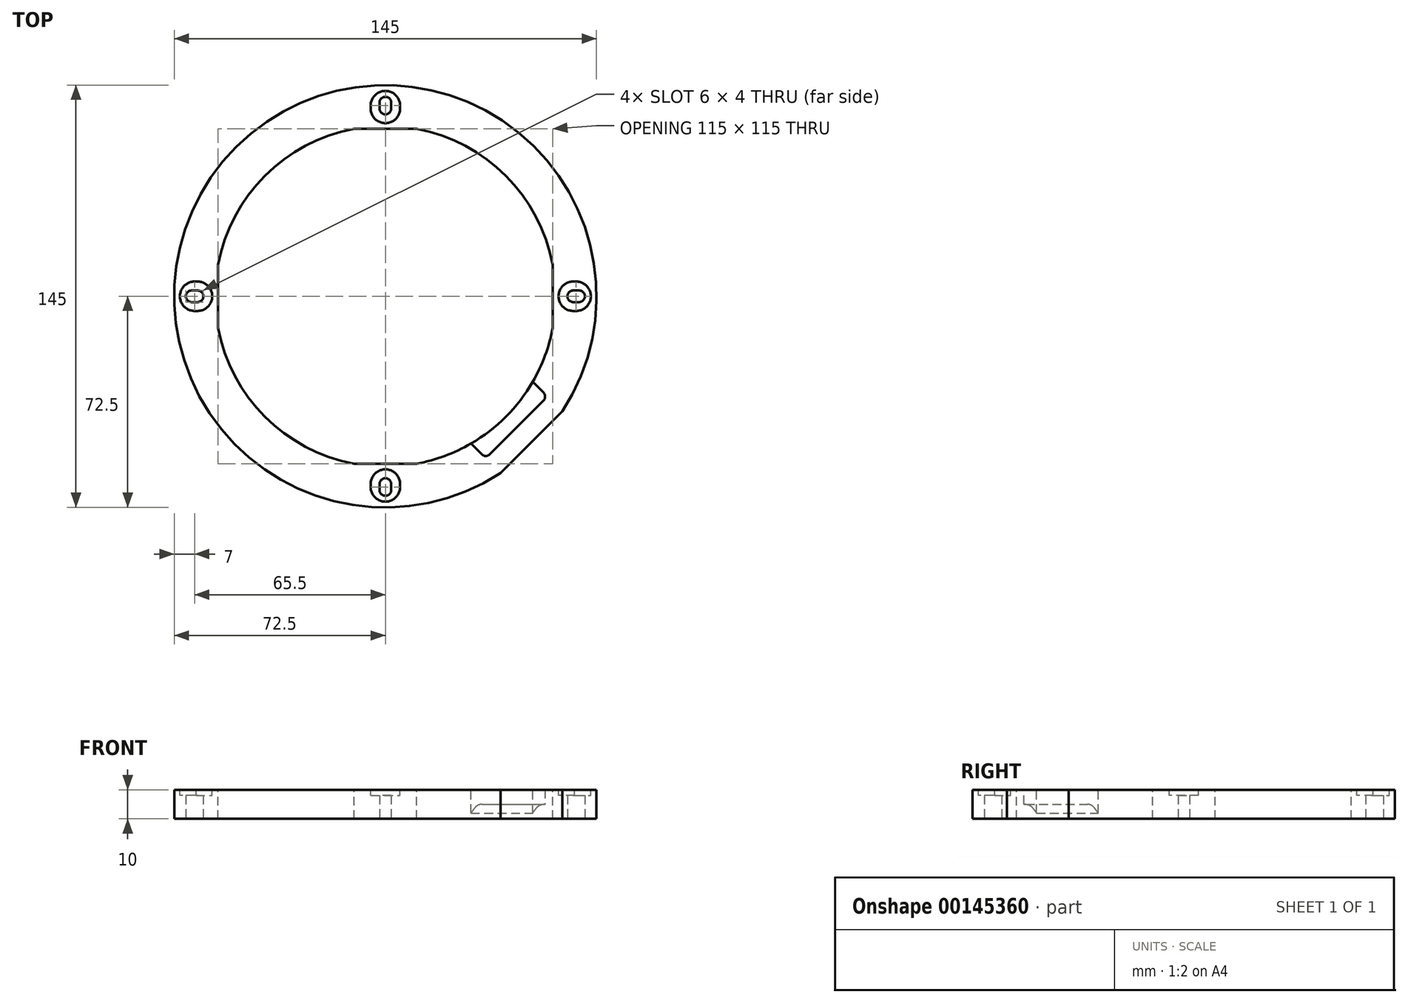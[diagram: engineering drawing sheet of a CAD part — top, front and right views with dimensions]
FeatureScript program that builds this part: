
annotation { "Feature Type Name" : "Feature", "Feature Type Description" : "" }
export const myFeature = defineFeature(function(context is Context, id is Id, definition is map)
    precondition{}
    {
        {
            var Q0;
            Q0=qCreatedBy(makeId("Top.planeOp"),FACE);
            var sketch = newSketch(context, id + "F0", { "sketchPlane" : qUnion([Q0])});
            skCircle(sketch, "E0", {"center": v(0, 0) * mm, "radius": 72.5 * mm});
            skCircle(sketch, "E1.0", {"center": v(0, 0) * mm, "radius": 58.5 * mm});
            skLineSegment(sketch, "E2", {"start": v(-72.5, 0) * mm, "end": v(-58.5, 0) * mm, "construction": true});
            skCircle(sketch, "E3", {"center": v(-65.5, 0) * mm, "radius": 2 * mm});
            skLineSegment(sketch, "E4", {"start": v(-67.5, 0) * mm, "end": v(-65.5, 0) * mm, "construction": true});
            skLineSegment(sketch, "E5", {"start": v(-65.5, 0) * mm, "end": v(-63.5, 0) * mm, "construction": true});
            skCircle(sketch, "E6", {"center": v(-66.5, 0) * mm, "radius": 2 * mm});
            skCircle(sketch, "E7", {"center": v(-64.5, 0) * mm, "radius": 2 * mm});
            skLineSegment(sketch, "E8.bottom", {"start": v(-64.5, 2) * mm, "end": v(-66.5, 2) * mm});
            skLineSegment(sketch, "E8.top", {"start": v(-64.5, -2) * mm, "end": v(-66.5, -2) * mm});
            skLineSegment(sketch, "E8.left", {"start": v(-64.5, 2) * mm, "end": v(-64.5, -2) * mm});
            skLineSegment(sketch, "E8.right", {"start": v(-66.5, 2) * mm, "end": v(-66.5, -2) * mm});
            skCircle(sketch, "E9.1.0", {"center": v(0, -66.5) * mm, "radius": 2 * mm});
            skCircle(sketch, "E9.1.1", {"center": v(0, -64.5) * mm, "radius": 2 * mm});
            skLineSegment(sketch, "E9.1.2", {"start": v(-2, -64.5) * mm, "end": v(-2, -66.5) * mm});
            skLineSegment(sketch, "E9.1.3", {"start": v(2, -64.5) * mm, "end": v(2, -66.5) * mm});
            skCircle(sketch, "E9.2.0", {"center": v(66.5, 0) * mm, "radius": 2 * mm});
            skCircle(sketch, "E9.2.1", {"center": v(64.5, 0) * mm, "radius": 2 * mm});
            skLineSegment(sketch, "E9.2.2", {"start": v(64.5, -2) * mm, "end": v(66.5, -2) * mm});
            skLineSegment(sketch, "E9.2.3", {"start": v(64.5, 2) * mm, "end": v(66.5, 2) * mm});
            skCircle(sketch, "E9.3.0", {"center": v(0, 66.5) * mm, "radius": 2 * mm});
            skCircle(sketch, "E9.3.1", {"center": v(0, 64.5) * mm, "radius": 2 * mm});
            skLineSegment(sketch, "E9.3.2", {"start": v(2, 64.5) * mm, "end": v(2, 66.5) * mm});
            skLineSegment(sketch, "E9.3.3", {"start": v(-2, 64.5) * mm, "end": v(-2, 66.5) * mm});
            skSolve(sketch);
        }
        {
            var Q0;
            Q0=makeQuery(id+"F0.imprint","IMPRINT",FACE,{"disambiguationData":[TD([[makeQuery(id+"F0.imprint","IMPRINT",EDGE,{"derivedFrom":sQuery(id+"F0.wireOp",EDGE,"E0")}),1.0]])]});
            extrude(context, id + "F1", {"entities" : qUnion([Q0]), "depth" : 10 * mm});
        }
        {
            var Q0;
            Q0=makeQuery(id+"F1.opExtrude","CAP_FACE",FACE,{"disambiguationData":[OSD([sQuery(id+"F0.wireOp",EDGE,"E0"),sQuery(id+"F0.wireOp",EDGE,"E1.0")])],"isStart":false});
            var sketch = newSketch(context, id + "F2", { "sketchPlane" : qUnion([Q0])});
            skLineSegment(sketch, "E10", {"start": v(0, 0) * mm, "end": v(51.27, -51.27) * mm, "construction": true});
            skLineSegment(sketch, "E11", {"start": v(40.66, -61.87) * mm, "end": v(61.87, -40.66) * mm});
            skLineSegment(sketch, "E12", {"start": v(40.66, -61.87) * mm, "end": v(39.55, -60.76) * mm});
            skLineSegment(sketch, "E13", {"start": v(39.55, -60.76) * mm, "end": v(60.76, -39.55) * mm});
            skLineSegment(sketch, "E14", {"start": v(60.76, -39.55) * mm, "end": v(61.87, -40.66) * mm});
            skSolve(sketch);
        }
        {
            var Q0;
            Q0 = qSketchRegion(id + "F2", true);
            var Q1;
            {var subQ0=sQuery(id+"F2.wireOp",EDGE,"E13");Q1=makeQuery(id+"F2.imprint","IMPRINT",FACE,{"disambiguationData":[TD([[makeQuery(id+"F2.imprint","IMPRINT",EDGE,{"derivedFrom":subQ0}),-1.0]])]});}
            extrude(context, id + "F3", {"entities" : qUnion([Q0, Q1]), "operationType" : NewBodyOperationType.REMOVE, "endBound" : BoundingType.THROUGH_ALL, "oppositeDirection" : true, "depth" : 25 * mm});
        }
        {
            var Q0;
            Q0=makeQuery(id+"F1.opExtrude","CAP_FACE",FACE,{"disambiguationData":[OSD([sQuery(id+"F0.wireOp",EDGE,"E0"),sQuery(id+"F0.wireOp",EDGE,"E1.0")])],"isStart":false});
            var sketch = newSketch(context, id + "F4", { "sketchPlane" : qUnion([Q0])});
            skLineSegment(sketch, "E15", {"start": v(60.76, -39.55) * mm, "end": v(50.59, -29.38) * mm, "construction": true});
            skLineSegment(sketch, "E16", {"start": v(50.59, -29.38) * mm, "end": v(29.38, -50.59) * mm});
            skLineSegment(sketch, "E17", {"start": v(29.38, -50.59) * mm, "end": v(39.55, -60.76) * mm, "construction": true});
            skLineSegment(sketch, "E18", {"start": v(39.55, -60.76) * mm, "end": v(60.76, -39.55) * mm, "construction": true});
            skLineSegment(sketch, "E19", {"start": v(34.46, -55.68) * mm, "end": v(55.68, -34.46) * mm});
            skLineSegment(sketch, "E20", {"start": v(55.68, -34.46) * mm, "end": v(50.59, -29.38) * mm});
            skLineSegment(sketch, "E21", {"start": v(34.46, -55.68) * mm, "end": v(29.38, -50.59) * mm});
            skSolve(sketch);
        }
        {
            var Q0;
            Q0 = qSketchRegion(id + "F4", true);
            extrude(context, id + "F5", {"entities" : qUnion([Q0]), "operationType" : NewBodyOperationType.REMOVE, "oppositeDirection" : true, "depth" : 5 * mm});
        }
        {
            var Q0;
            Q0=makeQuery(id+"F1.opExtrude","CAP_FACE",FACE,{"disambiguationData":[OSD([sQuery(id+"F0.wireOp",EDGE,"E0"),sQuery(id+"F0.wireOp",EDGE,"E1.0")])],"isStart":false});
            var sketch = newSketch(context, id + "F6", { "sketchPlane" : qUnion([Q0])});
            skCircle(sketch, "E22", {"center": v(-65.5, 0) * mm, "radius": 5.05 * mm});
            skPoint(sketch, "E22.centerSnap0", {"position": v(-62.5, 0) * mm});
            skPoint(sketch, "E22.centerSnap1", {"position": v(-65.5, 2) * mm});
            skCircle(sketch, "E23", {"center": v(0, 65.5) * mm, "radius": 5.05 * mm});
            skPoint(sketch, "E23.centerSnap0", {"position": v(-2, 65.5) * mm});
            skCircle(sketch, "E24", {"center": v(65.5, 0) * mm, "radius": 5.05 * mm});
            skPoint(sketch, "E24.centerSnap0", {"position": v(65.5, 2) * mm});
            skCircle(sketch, "E25", {"center": v(0, -65.5) * mm, "radius": 5.05 * mm});
            skPoint(sketch, "E25.centerSnap0", {"position": v(-2, -65.5) * mm});
            skPoint(sketch, "E25.centerSnap1", {"position": v(0, -62.5) * mm});
            skCircle(sketch, "E26", {"center": v(0, -64.5) * mm, "radius": 5.05 * mm});
            skCircle(sketch, "E27", {"center": v(-64.5, 0) * mm, "radius": 5.05 * mm});
            skCircle(sketch, "E28", {"center": v(0, 64.5) * mm, "radius": 5.05 * mm});
            skCircle(sketch, "E29", {"center": v(64.5, 0) * mm, "radius": 5.05 * mm});
            skSolve(sketch);
        }
        {
            var Q0;
            Q0 = qSketchRegion(id + "F6", true);
            extrude(context, id + "F7", {"entities" : qUnion([Q0]), "operationType" : NewBodyOperationType.REMOVE, "oppositeDirection" : true, "depth" : 2 * mm});
        }
        {
            var Q0;
            Q0=makeQuery(id+"F5.boolean.opBoolean","INTERSECT",EDGE,{"derivedFrom":[makeQuery(id+"F1.opExtrude","SWEPT_FACE",FACE,{"disambiguationData":[OSD([sQuery(id+"F0.wireOp",EDGE,"E1.0")])]}),makeQuery(id+"F5.opExtrude","CAP_FACE",FACE,{"disambiguationData":[OSD([sQuery(id+"F4.wireOp",EDGE,"E16"),sQuery(id+"F4.wireOp",EDGE,"E19"),sQuery(id+"F4.wireOp",EDGE,"E20"),sQuery(id+"F4.wireOp",EDGE,"E21")])],"isStart":false})]});
            chamfer(context, id + "F8", {"entities" : qUnion([Q0]), "width" : 3 * mm, "tangentPropagation" : true});
        }
        {
            var Q0;
            {var subQ0=makeQuery(id+"F5.opExtrude","CAP_FACE",FACE,{"disambiguationData":[OSD([sQuery(id+"F4.wireOp",EDGE,"E16"),sQuery(id+"F4.wireOp",EDGE,"E19"),sQuery(id+"F4.wireOp",EDGE,"E20"),sQuery(id+"F4.wireOp",EDGE,"E21")])],"isStart":false});Q0=makeQuery(id+"F8.opChamfer","BLEND_EDGE",EDGE,{"blendedFrom":[makeQuery(id+"F5.boolean.opBoolean","INTERSECT",EDGE,{"derivedFrom":[makeQuery(id+"F1.opExtrude","SWEPT_FACE",FACE,{"disambiguationData":[OSD([sQuery(id+"F0.wireOp",EDGE,"E1.0")])]}),subQ0]}),makeQuery(id+"F5.boolean.opBoolean","COPY",FACE,{"derivedFrom":subQ0})],"blendedInto":[makeQuery(id+"F5.boolean.opBoolean","COPY",FACE,{"derivedFrom":subQ0})]});}
            fillet(context, id + "F9", {"entities" : qUnion([Q0]), "radius" : 5 * mm, "tangentPropagation" : true, "allowEdgeOverflow" : false});
        }
        {
            var Q0;
            Q0=makeQuery(id+"F5.boolean.opBoolean","COPY",EDGE,{"derivedFrom":makeQuery(id+"F5.opExtrude","SWEPT_EDGE",EDGE,{"disambiguationData":[OSD([sQuery(id+"F4.wireOp",EDGE,"E19"),sQuery(id+"F4.wireOp",EDGE,"E20")])]})});
            var Q1;
            Q1=makeQuery(id+"F5.boolean.opBoolean","COPY",EDGE,{"derivedFrom":makeQuery(id+"F5.opExtrude","SWEPT_EDGE",EDGE,{"disambiguationData":[OSD([sQuery(id+"F4.wireOp",EDGE,"E19"),sQuery(id+"F4.wireOp",EDGE,"E21")])]})});
            fillet(context, id + "F10", {"entities" : qUnion([Q0, Q1]), "radius" : 2 * mm, "tangentPropagation" : true, "allowEdgeOverflow" : false});
        }
        {
            var Q0;
            Q0=makeQuery(id+"F1.opExtrude","CAP_FACE",FACE,{"disambiguationData":[OSD([sQuery(id+"F0.wireOp",EDGE,"E0"),sQuery(id+"F0.wireOp",EDGE,"E1.0"),sQuery(id+"F0.wireOp",EDGE,"E6"),sQuery(id+"F0.wireOp",EDGE,"E7"),sQuery(id+"F0.wireOp",EDGE,"E8.bottom"),sQuery(id+"F0.wireOp",EDGE,"E8.top"),sQuery(id+"F0.wireOp",EDGE,"E9.1.0"),sQuery(id+"F0.wireOp",EDGE,"E9.1.1"),sQuery(id+"F0.wireOp",EDGE,"E9.1.2"),sQuery(id+"F0.wireOp",EDGE,"E9.1.3"),sQuery(id+"F0.wireOp",EDGE,"E9.2.0"),sQuery(id+"F0.wireOp",EDGE,"E9.2.1"),sQuery(id+"F0.wireOp",EDGE,"E9.2.2"),sQuery(id+"F0.wireOp",EDGE,"E9.2.3"),sQuery(id+"F0.wireOp",EDGE,"E9.3.0"),sQuery(id+"F0.wireOp",EDGE,"E9.3.1"),sQuery(id+"F0.wireOp",EDGE,"E9.3.2"),sQuery(id+"F0.wireOp",EDGE,"E9.3.3")])],"isStart":false});
            var sketch = newSketch(context, id + "F11", { "sketchPlane" : qUnion([Q0])});
            skLineSegment(sketch, "E30.bottom", {"start": v(-10.77, -57.5) * mm, "end": v(10.77, -57.5) * mm});
            skLineSegment(sketch, "E30.top", {"start": v(-10.77, -58.5) * mm, "end": v(10.77, -58.5) * mm});
            skLineSegment(sketch, "E30.left", {"start": v(-10.77, -57.5) * mm, "end": v(-10.77, -58.5) * mm});
            skLineSegment(sketch, "E30.right", {"start": v(10.77, -57.5) * mm, "end": v(10.77, -58.5) * mm});
            skPoint(sketch, "E31.center", {"position": v(0, 0) * mm});
            skLineSegment(sketch, "E32.1.0", {"start": v(57.5, 10.77) * mm, "end": v(58.5, 10.77) * mm});
            skLineSegment(sketch, "E32.1.1", {"start": v(58.5, -10.77) * mm, "end": v(58.5, 10.77) * mm});
            skLineSegment(sketch, "E32.1.2", {"start": v(57.5, -10.77) * mm, "end": v(58.5, -10.77) * mm});
            skLineSegment(sketch, "E32.1.3", {"start": v(57.5, -10.77) * mm, "end": v(57.5, 10.77) * mm});
            skLineSegment(sketch, "E32.2.0", {"start": v(-10.77, 57.5) * mm, "end": v(-10.77, 58.5) * mm});
            skLineSegment(sketch, "E32.2.1", {"start": v(10.77, 58.5) * mm, "end": v(-10.77, 58.5) * mm});
            skLineSegment(sketch, "E32.2.2", {"start": v(10.77, 57.5) * mm, "end": v(10.77, 58.5) * mm});
            skLineSegment(sketch, "E32.2.3", {"start": v(10.77, 57.5) * mm, "end": v(-10.77, 57.5) * mm});
            skLineSegment(sketch, "E32.3.0", {"start": v(-57.5, -10.77) * mm, "end": v(-58.5, -10.77) * mm});
            skLineSegment(sketch, "E32.3.1", {"start": v(-58.5, 10.77) * mm, "end": v(-58.5, -10.77) * mm});
            skLineSegment(sketch, "E32.3.2", {"start": v(-57.5, 10.77) * mm, "end": v(-58.5, 10.77) * mm});
            skLineSegment(sketch, "E32.3.3", {"start": v(-57.5, 10.77) * mm, "end": v(-57.5, -10.77) * mm});
            skSolve(sketch);
        }
        {
            var Q0;
            Q0 = qSketchRegion(id + "F11", true);
            extrude(context, id + "F12", {"entities" : qUnion([Q0]), "operationType" : NewBodyOperationType.ADD, "oppositeDirection" : true, "depth" : 10 * mm});
        }
    });
